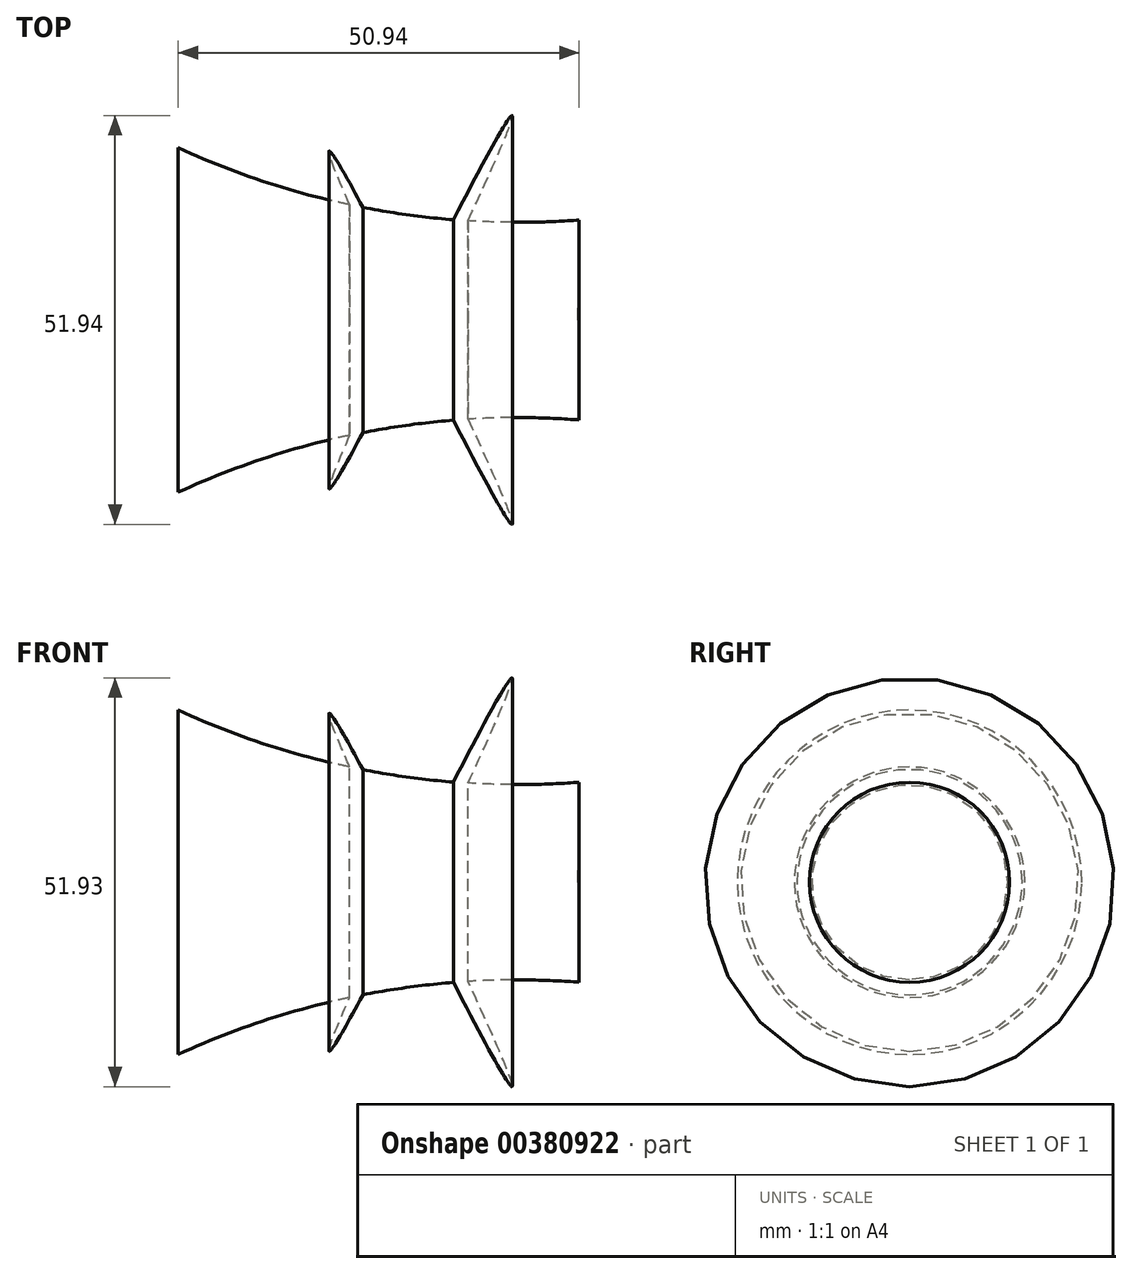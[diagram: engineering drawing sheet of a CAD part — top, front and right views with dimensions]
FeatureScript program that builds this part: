
annotation { "Feature Type Name" : "Feature", "Feature Type Description" : "" }
export const myFeature = defineFeature(function(context is Context, id is Id, definition is map)
    precondition{}
    {
        {
            var Q0;
            Q0=qCreatedBy(makeId("Top.planeOp"),FACE);
            var sketch = newSketch(context, id + "F0", { "sketchPlane" : qUnion([Q0])});
            skArc(sketch, "E0", {"start": v(50.94, -12.7) * mm, "mid": v(24.88, -14.04) * mm, "end": v(0, -21.88) * mm});
            skArc(sketch, "E1", {"start": v(0, 21.59) * mm, "mid": v(24.63, 13.17) * mm, "end": v(50.66, 12.7) * mm});
            skLineSegment(sketch, "E2", {"start": v(50.94, -12.7) * mm, "end": v(50.66, 12.7) * mm});
            skLineSegment(sketch, "E3", {"start": v(50.8, 0) * mm, "end": v(0, 0) * mm});
            skLineSegment(sketch, "E4", {"start": v(0, -21.88) * mm, "end": v(0, 21.59) * mm});
            skEllipse(sketch, "E5", {"center": v(30.8, -2.24) * mm, "majorRadius": 26.4 * mm, "minorRadius": 0.95 * mm, "majorAxis": v(0.44, -0.9)});
            skSolve(sketch);
        }
        {
            var Q0;
            {var subQ0=sQuery(id+"F0.wireOp",EDGE,"E0");Q0=makeQuery(id+"F0.imprint","IMPRINT",FACE,{"disambiguationData":[TD([[makeQuery(id+"F0.imprint","IMPRINT",EDGE,{"derivedFrom":subQ0}),-1.0]])]});}
            var Q1;
            Q1=sQuery(id+"F0.wireOp",EDGE,"E3");
            revolve(context, id + "F1", {"entities" : qUnion([Q0]), "axis" : qUnion([Q1]), "revolveType" : RevolveType.FULL});
        }
        {
            var Q0;
            {var subQ0=sQuery(id+"F0.wireOp",EDGE,"E5");var subQ1=sQuery(id+"F0.wireOp",EDGE,"E0");var subQ2=makeQuery(id+"F0.imprint","INTERSECT",VERTEX,{"disambiguationData":[OD(0.0)],"derivedFrom":[subQ1,subQ0]});Q0=makeQuery(id+"F0.imprint","IMPRINT",FACE,{"disambiguationData":[TD([[makeQuery(id+"F0.imprint","IMPRINT",EDGE,{"disambiguationData":[TD([[subQ2,-1.0]])],"derivedFrom":subQ1}),1.0]])]});}
            var Q1;
            {var subQ0=sQuery(id+"F0.wireOp",EDGE,"E5");var subQ1=sQuery(id+"F0.wireOp",EDGE,"E1");var subQ2=makeQuery(id+"F0.imprint","INTERSECT",VERTEX,{"disambiguationData":[OD(0.0)],"derivedFrom":[subQ1,subQ0]});Q1=makeQuery(id+"F0.imprint","IMPRINT",FACE,{"disambiguationData":[TD([[makeQuery(id+"F0.imprint","IMPRINT",EDGE,{"disambiguationData":[TD([[subQ2,-1.0]])],"derivedFrom":subQ1}),1.0]])]});}
            var Q2;
            Q2=sQuery(id+"F0.wireOp",EDGE,"E3");
            revolve(context, id + "F2", {"operationType" : NewBodyOperationType.ADD, "entities" : qUnion([Q0, Q1]), "axis" : qUnion([Q2]), "revolveType" : RevolveType.FULL});
        }
    });
